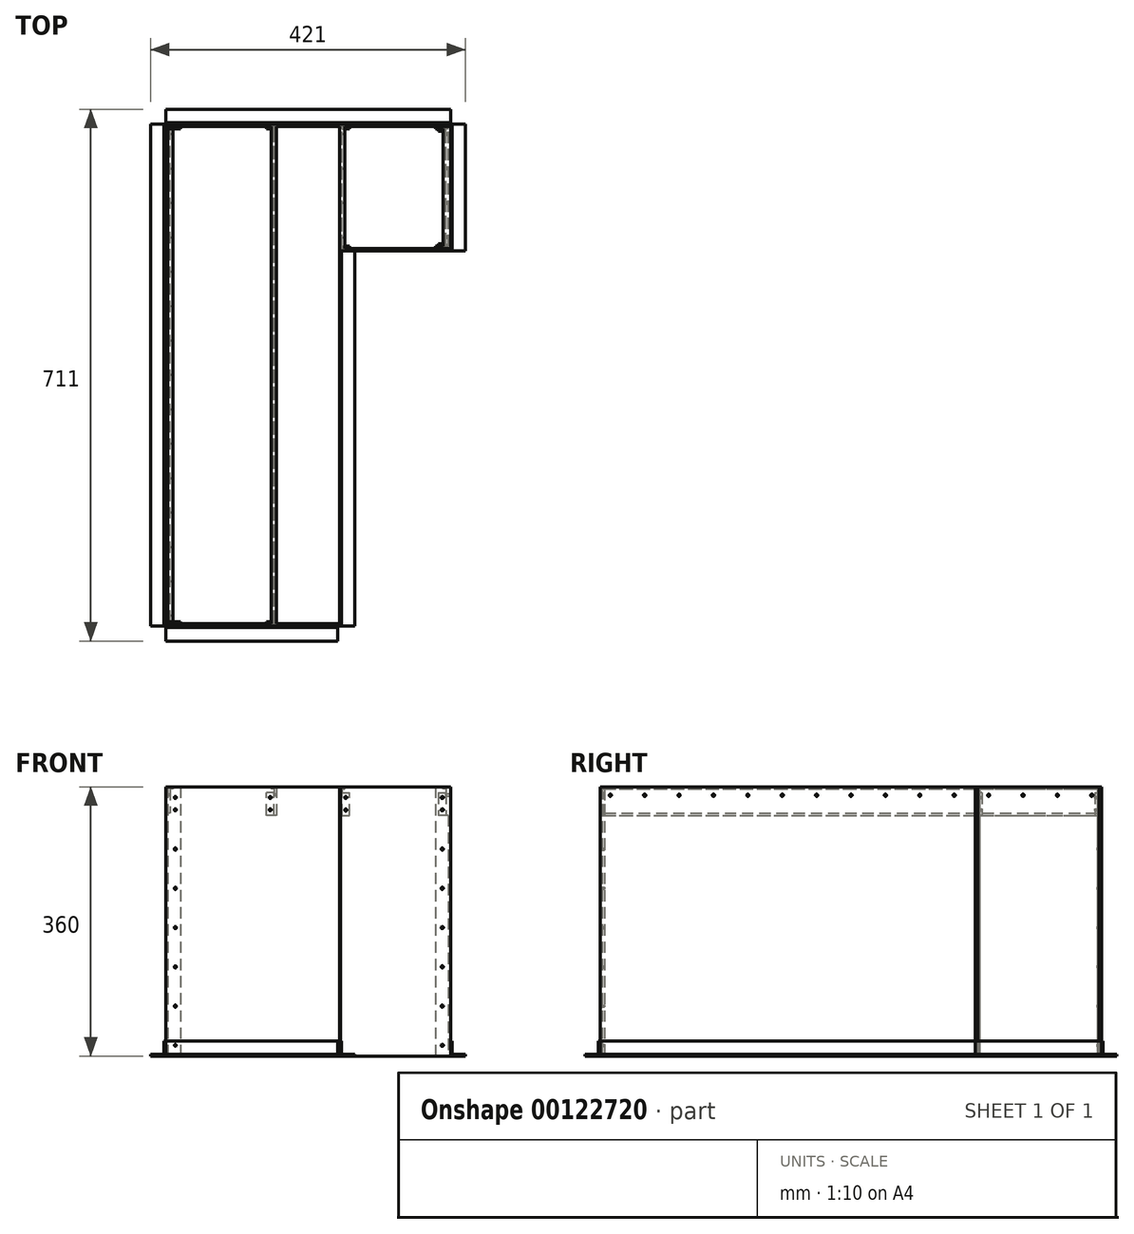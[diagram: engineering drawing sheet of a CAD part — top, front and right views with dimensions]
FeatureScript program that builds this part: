
annotation { "Feature Type Name" : "Feature", "Feature Type Description" : "" }
export const myFeature = defineFeature(function(context is Context, id is Id, definition is map)
    precondition{}
    {
        {
            var Q0;
            Q0=qCreatedBy(makeId("Top.planeOp"),FACE);
            var sketch = newSketch(context, id + "F0", { "sketchPlane" : qUnion([Q0])});
            skLineSegment(sketch, "E0.bottom", {"start": v(0, 0) * mm, "end": v(381, 0) * mm});
            skLineSegment(sketch, "E0.top", {"start": v(0, -3) * mm, "end": v(381, -3) * mm});
            skLineSegment(sketch, "E0.left", {"start": v(0, 0) * mm, "end": v(0, -3) * mm});
            skLineSegment(sketch, "E0.right", {"start": v(381, 0) * mm, "end": v(381, -3) * mm});
            skLineSegment(sketch, "E1.bottom", {"start": v(3, -3) * mm, "end": v(148, -3) * mm, "construction": true});
            skLineSegment(sketch, "E1.top", {"start": v(3, -78) * mm, "end": v(148, -78) * mm, "construction": true});
            skLineSegment(sketch, "E1.left", {"start": v(3, -3) * mm, "end": v(3, -78) * mm, "construction": true});
            skLineSegment(sketch, "E1.right", {"start": v(148, -3) * mm, "end": v(148, -78) * mm, "construction": true});
            skLineSegment(sketch, "E2.bottom", {"start": v(233, -3) * mm, "end": v(378, -3) * mm, "construction": true});
            skLineSegment(sketch, "E2.top", {"start": v(233, -58) * mm, "end": v(378, -58) * mm, "construction": true});
            skLineSegment(sketch, "E2.left", {"start": v(233, -3) * mm, "end": v(233, -58) * mm, "construction": true});
            skLineSegment(sketch, "E2.right", {"start": v(378, -3) * mm, "end": v(378, -58) * mm, "construction": true});
            skSolve(sketch);
        }
        {
            var Q0;
            Q0=qCreatedBy(makeId("Top.planeOp"),FACE);
            var sketch = newSketch(context, id + "F1", { "sketchPlane" : qUnion([Q0])});
            skLineSegment(sketch, "E3.bottom", {"start": v(3, -668) * mm, "end": v(0, -668) * mm});
            skLineSegment(sketch, "E3.top", {"start": v(3, -3) * mm, "end": v(0, -3) * mm});
            skLineSegment(sketch, "E3.left", {"start": v(3, -668) * mm, "end": v(3, -3) * mm});
            skLineSegment(sketch, "E3.right", {"start": v(0, -668) * mm, "end": v(0, -3) * mm});
            skLineSegment(sketch, "E4.bottom", {"start": v(3, -3) * mm, "end": v(20, -3) * mm});
            skLineSegment(sketch, "E4.top", {"start": v(3, -6) * mm, "end": v(20, -6) * mm});
            skLineSegment(sketch, "E4.left", {"start": v(3, -3) * mm, "end": v(3, -6) * mm});
            skLineSegment(sketch, "E4.right", {"start": v(20, -3) * mm, "end": v(20, -6) * mm});
            skLineSegment(sketch, "E5.bottom", {"start": v(3, -668) * mm, "end": v(20, -668) * mm});
            skLineSegment(sketch, "E5.top", {"start": v(3, -665) * mm, "end": v(20, -665) * mm});
            skLineSegment(sketch, "E5.left", {"start": v(3, -668) * mm, "end": v(3, -665) * mm});
            skLineSegment(sketch, "E5.right", {"start": v(20, -668) * mm, "end": v(20, -665) * mm});
            skSolve(sketch);
        }
        {
            var Q0;
            Q0=qCreatedBy(makeId("Top.planeOp"),FACE);
            var sketch = newSketch(context, id + "F2", { "sketchPlane" : qUnion([Q0])});
            skLineSegment(sketch, "E6.bottom", {"start": v(148, -3) * mm, "end": v(233, -3) * mm});
            skLineSegment(sketch, "E6.top", {"start": v(148, -399) * mm, "end": v(233, -399) * mm});
            skLineSegment(sketch, "E6.left", {"start": v(148, -3) * mm, "end": v(148, -399) * mm});
            skLineSegment(sketch, "E6.right", {"start": v(233, -3) * mm, "end": v(233, -399) * mm});
            skLineSegment(sketch, "E7.bottom", {"start": v(161.5, -6) * mm, "end": v(219.5, -6) * mm, "construction": true});
            skLineSegment(sketch, "E7.top", {"start": v(161.5, -67) * mm, "end": v(219.5, -67) * mm, "construction": true});
            skLineSegment(sketch, "E7.left", {"start": v(161.5, -6) * mm, "end": v(161.5, -67) * mm, "construction": true});
            skLineSegment(sketch, "E7.right", {"start": v(219.5, -6) * mm, "end": v(219.5, -67) * mm, "construction": true});
            skLineSegment(sketch, "E8.bottom", {"start": v(148, -400) * mm, "end": v(233, -400) * mm});
            skLineSegment(sketch, "E8.top", {"start": v(148, -668) * mm, "end": v(233, -668) * mm});
            skLineSegment(sketch, "E8.left", {"start": v(148, -400) * mm, "end": v(148, -668) * mm});
            skLineSegment(sketch, "E8.right", {"start": v(233, -400) * mm, "end": v(233, -668) * mm});
            skSolve(sketch);
        }
        {
            var Q0;
            Q0=qCreatedBy(makeId("Top.planeOp"),FACE);
            var sketch = newSketch(context, id + "F3", { "sketchPlane" : qUnion([Q0])});
            skLineSegment(sketch, "E9.bottom", {"start": v(381, -3) * mm, "end": v(378, -3) * mm});
            skLineSegment(sketch, "E9.top", {"start": v(381, -166) * mm, "end": v(378, -166) * mm});
            skLineSegment(sketch, "E9.left", {"start": v(381, -3) * mm, "end": v(381, -166) * mm});
            skLineSegment(sketch, "E9.right", {"start": v(378, -3) * mm, "end": v(378, -166) * mm});
            skLineSegment(sketch, "E10.bottom", {"start": v(378, -3) * mm, "end": v(361, -3) * mm});
            skLineSegment(sketch, "E10.top", {"start": v(378, -6) * mm, "end": v(361, -6) * mm});
            skLineSegment(sketch, "E10.left", {"start": v(378, -3) * mm, "end": v(378, -6) * mm});
            skLineSegment(sketch, "E10.right", {"start": v(361, -3) * mm, "end": v(361, -6) * mm});
            skLineSegment(sketch, "E11.bottom", {"start": v(378, -166) * mm, "end": v(361, -166) * mm});
            skLineSegment(sketch, "E11.top", {"start": v(378, -163) * mm, "end": v(361, -163) * mm});
            skLineSegment(sketch, "E11.left", {"start": v(378, -166) * mm, "end": v(378, -163) * mm});
            skLineSegment(sketch, "E11.right", {"start": v(361, -166) * mm, "end": v(361, -163) * mm});
            skSolve(sketch);
        }
        {
            var Q0;
            Q0=qCreatedBy(makeId("Top.planeOp"),FACE);
            var sketch = newSketch(context, id + "F4", { "sketchPlane" : qUnion([Q0])});
            skLineSegment(sketch, "E12.bottom", {"start": v(0, -668) * mm, "end": v(233, -668) * mm});
            skLineSegment(sketch, "E12.top", {"start": v(0, -671) * mm, "end": v(233, -671) * mm});
            skLineSegment(sketch, "E12.left", {"start": v(0, -668) * mm, "end": v(0, -671) * mm});
            skLineSegment(sketch, "E12.right", {"start": v(233, -668) * mm, "end": v(233, -671) * mm});
            skSolve(sketch);
        }
        {
            var Q0;
            Q0=qCreatedBy(makeId("Top.planeOp"),FACE);
            var sketch = newSketch(context, id + "F5", { "sketchPlane" : qUnion([Q0])});
            skLineSegment(sketch, "E13.bottom", {"start": v(233, -166) * mm, "end": v(381, -166) * mm});
            skLineSegment(sketch, "E13.top", {"start": v(233, -169) * mm, "end": v(381, -169) * mm});
            skLineSegment(sketch, "E13.left", {"start": v(233, -166) * mm, "end": v(233, -169) * mm});
            skLineSegment(sketch, "E13.right", {"start": v(381, -166) * mm, "end": v(381, -169) * mm});
            skSolve(sketch);
        }
        {
            var Q0;
            Q0=qCreatedBy(makeId("Top.planeOp"),FACE);
            var sketch = newSketch(context, id + "F6", { "sketchPlane" : qUnion([Q0])});
            skLineSegment(sketch, "E14.bottom", {"start": v(145, -3) * mm, "end": v(125, -3) * mm});
            skLineSegment(sketch, "E14.top", {"start": v(145, -6) * mm, "end": v(125, -6) * mm});
            skLineSegment(sketch, "E14.left", {"start": v(145, -3) * mm, "end": v(145, -6) * mm});
            skLineSegment(sketch, "E14.right", {"start": v(125, -3) * mm, "end": v(125, -6) * mm});
            skLineSegment(sketch, "E15.bottom", {"start": v(145, -6) * mm, "end": v(142, -6) * mm});
            skLineSegment(sketch, "E15.top", {"start": v(145, -668) * mm, "end": v(142, -668) * mm});
            skLineSegment(sketch, "E15.left", {"start": v(145, -6) * mm, "end": v(145, -668) * mm});
            skLineSegment(sketch, "E15.right", {"start": v(142, -6) * mm, "end": v(142, -668) * mm});
            skLineSegment(sketch, "E16.bottom", {"start": v(142, -668) * mm, "end": v(125, -668) * mm});
            skLineSegment(sketch, "E16.top", {"start": v(142, -665) * mm, "end": v(125, -665) * mm});
            skLineSegment(sketch, "E16.left", {"start": v(142, -668) * mm, "end": v(142, -665) * mm});
            skLineSegment(sketch, "E16.right", {"start": v(125, -668) * mm, "end": v(125, -665) * mm});
            skSolve(sketch);
        }
        {
            var Q0;
            Q0=makeQuery(id+"F0.imprint","IMPRINT",FACE,{"disambiguationData":[TD([[makeQuery(id+"F0.imprint","IMPRINT",EDGE,{"derivedFrom":sQuery(id+"F0.wireOp",EDGE,"E0.bottom")}),-1.0]])]});
            var Q1;
            Q1=makeQuery(id+"F1.imprint","IMPRINT",FACE,{"disambiguationData":[TD([[makeQuery(id+"F1.imprint","IMPRINT",EDGE,{"derivedFrom":sQuery(id+"F1.wireOp",EDGE,"E4.bottom")}),-1.0]])]});
            var Q2;
            Q2=makeQuery(id+"F1.imprint","IMPRINT",FACE,{"disambiguationData":[TD([[makeQuery(id+"F1.imprint","IMPRINT",EDGE,{"derivedFrom":sQuery(id+"F1.wireOp",EDGE,"E5.bottom")}),1.0]])]});
            var Q3;
            Q3=makeQuery(id+"F1.imprint","IMPRINT",FACE,{"disambiguationData":[TD([[makeQuery(id+"F1.imprint","IMPRINT",EDGE,{"derivedFrom":sQuery(id+"F1.wireOp",EDGE,"E3.bottom")}),-1.0]])]});
            var Q4;
            Q4=makeQuery(id+"F3.imprint","IMPRINT",FACE,{"disambiguationData":[TD([[makeQuery(id+"F3.imprint","IMPRINT",EDGE,{"derivedFrom":sQuery(id+"F3.wireOp",EDGE,"E10.bottom")}),1.0]])]});
            var Q5;
            Q5=makeQuery(id+"F3.imprint","IMPRINT",FACE,{"disambiguationData":[TD([[makeQuery(id+"F3.imprint","IMPRINT",EDGE,{"derivedFrom":sQuery(id+"F3.wireOp",EDGE,"E11.bottom")}),-1.0]])]});
            var Q6;
            Q6=makeQuery(id+"F3.imprint","IMPRINT",FACE,{"disambiguationData":[TD([[makeQuery(id+"F3.imprint","IMPRINT",EDGE,{"derivedFrom":sQuery(id+"F3.wireOp",EDGE,"E9.bottom")}),1.0]])]});
            var Q7;
            Q7=makeQuery(id+"F4.imprint","IMPRINT",FACE,{"disambiguationData":[TD([[makeQuery(id+"F4.imprint","IMPRINT",EDGE,{"derivedFrom":sQuery(id+"F4.wireOp",EDGE,"E12.bottom")}),-1.0]])]});
            var Q8;
            Q8=makeQuery(id+"F5.imprint","IMPRINT",FACE,{"disambiguationData":[TD([[makeQuery(id+"F5.imprint","IMPRINT",EDGE,{"derivedFrom":sQuery(id+"F5.wireOp",EDGE,"E13.bottom")}),-1.0]])]});
            extrude(context, id + "F7", {"entities" : qUnion([Q0, Q1, Q2, Q3, Q4, Q5, Q6, Q7, Q8]), "depth" : 360 * mm});
        }
        {
            var Q0;
            Q0=makeQuery(id+"F7.opExtrude","SWEPT_FACE",FACE,{"disambiguationData":[OSD([sQuery(id+"F0.wireOp",EDGE,"E0.bottom")])]});
            var sketch = newSketch(context, id + "F8", { "sketchPlane" : qUnion([Q0])});
            skLineSegment(sketch, "E17.bottom", {"start": v(0, 0) * mm, "end": v(2, 0) * mm});
            skLineSegment(sketch, "E17.top", {"start": v(0, 20) * mm, "end": v(2, 20) * mm});
            skLineSegment(sketch, "E17.left", {"start": v(0, 0) * mm, "end": v(0, 20) * mm});
            skLineSegment(sketch, "E17.right", {"start": v(2, 0) * mm, "end": v(2, 20) * mm});
            skLineSegment(sketch, "E18.bottom", {"start": v(2, 0) * mm, "end": v(20, 0) * mm});
            skLineSegment(sketch, "E18.top", {"start": v(2, 2) * mm, "end": v(20, 2) * mm});
            skLineSegment(sketch, "E18.left", {"start": v(2, 0) * mm, "end": v(2, 2) * mm});
            skLineSegment(sketch, "E18.right", {"start": v(20, 0) * mm, "end": v(20, 2) * mm});
            skSolve(sketch);
        }
        {
            var Q0;
            Q0=qSketchRegion(id+"F8",true);
            extrude(context, id + "F9", {"entities" : qUnion([Q0]), "oppositeDirection" : true, "depth" : 671 * mm});
        }
        {
            var Q0;
            Q0=makeQuery(id+"F7.opExtrude","SWEPT_FACE",FACE,{"disambiguationData":[OSD([sQuery(id+"F1.wireOp",EDGE,"E3.right")])]});
            var sketch = newSketch(context, id + "F10", { "sketchPlane" : qUnion([Q0])});
            skLineSegment(sketch, "E19.bottom", {"start": v(671, 20) * mm, "end": v(673, 20) * mm});
            skLineSegment(sketch, "E19.top", {"start": v(671, 0) * mm, "end": v(673, 0) * mm});
            skLineSegment(sketch, "E19.left", {"start": v(671, 20) * mm, "end": v(671, 0) * mm});
            skLineSegment(sketch, "E19.right", {"start": v(673, 20) * mm, "end": v(673, 0) * mm});
            skLineSegment(sketch, "E20.bottom", {"start": v(673, 0) * mm, "end": v(691, 0) * mm});
            skLineSegment(sketch, "E20.top", {"start": v(673, 2) * mm, "end": v(691, 2) * mm});
            skLineSegment(sketch, "E20.left", {"start": v(673, 0) * mm, "end": v(673, 2) * mm});
            skLineSegment(sketch, "E20.right", {"start": v(691, 0) * mm, "end": v(691, 2) * mm});
            skSolve(sketch);
        }
        {
            var Q0;
            Q0=qSketchRegion(id+"F10",true);
            extrude(context, id + "F11", {"entities" : qUnion([Q0]), "operationType" : NewBodyOperationType.ADD, "oppositeDirection" : true, "depth" : 230 * mm});
        }
        {
            var Q0;
            Q0=makeQuery(id+"F7.opExtrude","SWEPT_FACE",FACE,{"disambiguationData":[OSD([sQuery(id+"F4.wireOp",EDGE,"E12.top")])]});
            var sketch = newSketch(context, id + "F12", { "sketchPlane" : qUnion([Q0])});
            skLineSegment(sketch, "E21.bottom", {"start": v(233, 0) * mm, "end": v(235, 0) * mm});
            skLineSegment(sketch, "E21.top", {"start": v(233, 20) * mm, "end": v(235, 20) * mm});
            skLineSegment(sketch, "E21.left", {"start": v(233, 0) * mm, "end": v(233, 20) * mm});
            skLineSegment(sketch, "E21.right", {"start": v(235, 0) * mm, "end": v(235, 20) * mm});
            skLineSegment(sketch, "E22.bottom", {"start": v(235, 0) * mm, "end": v(253, 0) * mm});
            skLineSegment(sketch, "E22.top", {"start": v(235, 2) * mm, "end": v(253, 2) * mm});
            skLineSegment(sketch, "E22.left", {"start": v(235, 0) * mm, "end": v(235, 2) * mm});
            skLineSegment(sketch, "E22.right", {"start": v(253, 0) * mm, "end": v(253, 2) * mm});
            skSolve(sketch);
        }
        {
            var Q0;
            Q0=qSketchRegion(id+"F12",true);
            extrude(context, id + "F13", {"entities" : qUnion([Q0]), "oppositeDirection" : true, "depth" : 502 * mm});
        }
        {
            var Q0;
            Q0=makeQuery(id+"F7.opExtrude","SWEPT_FACE",FACE,{"disambiguationData":[OSD([sQuery(id+"F5.wireOp",EDGE,"E13.top")])]});
            var sketch = newSketch(context, id + "F14", { "sketchPlane" : qUnion([Q0])});
            skLineSegment(sketch, "E23.bottom", {"start": v(381, 0) * mm, "end": v(383, 0) * mm});
            skLineSegment(sketch, "E23.top", {"start": v(381, 20) * mm, "end": v(383, 20) * mm});
            skLineSegment(sketch, "E23.left", {"start": v(381, 0) * mm, "end": v(381, 20) * mm});
            skLineSegment(sketch, "E23.right", {"start": v(383, 0) * mm, "end": v(383, 20) * mm});
            skLineSegment(sketch, "E24.bottom", {"start": v(383, 0) * mm, "end": v(401, 0) * mm});
            skLineSegment(sketch, "E24.top", {"start": v(383, 2) * mm, "end": v(401, 2) * mm});
            skLineSegment(sketch, "E24.left", {"start": v(383, 0) * mm, "end": v(383, 2) * mm});
            skLineSegment(sketch, "E24.right", {"start": v(401, 0) * mm, "end": v(401, 2) * mm});
            skSolve(sketch);
        }
        {
            var Q0;
            Q0=qSketchRegion(id+"F14",true);
            extrude(context, id + "F15", {"entities" : qUnion([Q0]), "oppositeDirection" : true, "depth" : 169 * mm});
        }
        {
            var Q0;
            Q0=makeQuery(id+"F7.opExtrude","SWEPT_FACE",FACE,{"disambiguationData":[OSD([sQuery(id+"F0.wireOp",EDGE,"E0.right")])]});
            var sketch = newSketch(context, id + "F16", { "sketchPlane" : qUnion([Q0])});
            skLineSegment(sketch, "E25.bottom", {"start": v(0, 0) * mm, "end": v(2, 0) * mm});
            skLineSegment(sketch, "E25.top", {"start": v(0, 20) * mm, "end": v(2, 20) * mm});
            skLineSegment(sketch, "E25.left", {"start": v(0, 0) * mm, "end": v(0, 20) * mm});
            skLineSegment(sketch, "E25.right", {"start": v(2, 0) * mm, "end": v(2, 20) * mm});
            skLineSegment(sketch, "E26.bottom", {"start": v(2, 0) * mm, "end": v(20, 0) * mm});
            skLineSegment(sketch, "E26.top", {"start": v(2, 2) * mm, "end": v(20, 2) * mm});
            skLineSegment(sketch, "E26.left", {"start": v(2, 0) * mm, "end": v(2, 2) * mm});
            skLineSegment(sketch, "E26.right", {"start": v(20, 0) * mm, "end": v(20, 2) * mm});
            skSolve(sketch);
        }
        {
            var Q0;
            Q0=qSketchRegion(id+"F16",true);
            extrude(context, id + "F17", {"entities" : qUnion([Q0]), "oppositeDirection" : true, "depth" : 381 * mm});
        }
        {
            var Q0;
            Q0=makeQuery(id+"F7.opExtrude","CAP_FACE",FACE,{"disambiguationData":[OSD([sQuery(id+"F4.wireOp",EDGE,"E12.bottom"),sQuery(id+"F4.wireOp",EDGE,"E12.top"),sQuery(id+"F4.wireOp",EDGE,"E12.left"),sQuery(id+"F4.wireOp",EDGE,"E12.right")])],"isStart":false});
            var sketch = newSketch(context, id + "F18", { "sketchPlane" : qUnion([Q0])});
            skLineSegment(sketch, "E27.bottom", {"start": v(233, -169) * mm, "end": v(234, -169) * mm});
            skLineSegment(sketch, "E27.top", {"start": v(233, -671) * mm, "end": v(234, -671) * mm});
            skLineSegment(sketch, "E27.left", {"start": v(233, -169) * mm, "end": v(233, -671) * mm});
            skLineSegment(sketch, "E27.right", {"start": v(234, -169) * mm, "end": v(234, -671) * mm});
            skSolve(sketch);
        }
        {
            var Q0;
            Q0=qSketchRegion(id+"F18",true);
            extrude(context, id + "F19", {"entities" : qUnion([Q0]), "oppositeDirection" : true, "depth" : 360 * mm});
        }
        {
            var Q0;
            Q0=makeQuery(id+"F7.opExtrude","SWEPT_FACE",FACE,{"disambiguationData":[OSD([sQuery(id+"F1.wireOp",EDGE,"E4.top")])]});
            var sketch = newSketch(context, id + "F20", { "sketchPlane" : qUnion([Q0])});
            skLineSegment(sketch, "E28.bottom", {"start": v(10, 360) * mm, "end": v(6, 360) * mm});
            skLineSegment(sketch, "E28.top", {"start": v(10, 357) * mm, "end": v(6, 357) * mm});
            skLineSegment(sketch, "E28.left", {"start": v(10, 360) * mm, "end": v(10, 357) * mm});
            skLineSegment(sketch, "E28.right", {"start": v(6, 360) * mm, "end": v(6, 357) * mm});
            skLineSegment(sketch, "E29.bottom", {"start": v(6, 360) * mm, "end": v(3, 360) * mm});
            skLineSegment(sketch, "E29.top", {"start": v(6, 325) * mm, "end": v(3, 325) * mm});
            skLineSegment(sketch, "E29.left", {"start": v(6, 360) * mm, "end": v(6, 325) * mm});
            skLineSegment(sketch, "E29.right", {"start": v(3, 360) * mm, "end": v(3, 325) * mm});
            skSolve(sketch);
        }
        {
            var Q0;
            Q0=qSketchRegion(id+"F20",true);
            extrude(context, id + "F21", {"entities" : qUnion([Q0]), "depth" : 659 * mm});
        }
        {
            var Q0;
            Q0=makeQuery(id+"F7.opExtrude","SWEPT_FACE",FACE,{"disambiguationData":[OSD([sQuery(id+"F0.wireOp",EDGE,"E0.top")])]});
            var sketch = newSketch(context, id + "F22", { "sketchPlane" : qUnion([Q0])});
            skLineSegment(sketch, "E30.bottom", {"start": v(148, 360) * mm, "end": v(141, 360) * mm});
            skLineSegment(sketch, "E30.top", {"start": v(148, 357) * mm, "end": v(141, 357) * mm});
            skLineSegment(sketch, "E30.left", {"start": v(148, 360) * mm, "end": v(148, 357) * mm});
            skLineSegment(sketch, "E30.right", {"start": v(141, 360) * mm, "end": v(141, 357) * mm});
            skLineSegment(sketch, "E31.bottom", {"start": v(148, 357) * mm, "end": v(145, 357) * mm});
            skLineSegment(sketch, "E31.top", {"start": v(148, 322) * mm, "end": v(145, 322) * mm});
            skLineSegment(sketch, "E31.left", {"start": v(148, 357) * mm, "end": v(148, 322) * mm});
            skLineSegment(sketch, "E31.right", {"start": v(145, 357) * mm, "end": v(145, 322) * mm});
            skSolve(sketch);
        }
        {
            var Q0;
            Q0=qSketchRegion(id+"F22",true);
            extrude(context, id + "F23", {"entities" : qUnion([Q0]), "depth" : 665 * mm});
        }
        {
            var Q0;
            Q0=makeQuery(id+"F7.opExtrude","SWEPT_FACE",FACE,{"disambiguationData":[OSD([sQuery(id+"F0.wireOp",EDGE,"E0.top")])]});
            var sketch = newSketch(context, id + "F24", { "sketchPlane" : qUnion([Q0])});
            skLineSegment(sketch, "E32.bottom", {"start": v(145, 322) * mm, "end": v(135, 322) * mm});
            skLineSegment(sketch, "E32.top", {"start": v(145, 352) * mm, "end": v(135, 352) * mm});
            skLineSegment(sketch, "E32.left", {"start": v(145, 322) * mm, "end": v(145, 352) * mm});
            skLineSegment(sketch, "E32.right", {"start": v(135, 322) * mm, "end": v(135, 352) * mm});
            skSolve(sketch);
        }
        {
            var Q0;
            Q0=qSketchRegion(id+"F24",true);
            extrude(context, id + "F25", {"entities" : qUnion([Q0]), "operationType" : NewBodyOperationType.ADD, "depth" : 3 * mm});
        }
        {
            var Q0;
            Q0=makeQuery(id+"F7.opExtrude","SWEPT_FACE",FACE,{"disambiguationData":[OSD([sQuery(id+"F4.wireOp",EDGE,"E12.bottom")])]});
            var sketch = newSketch(context, id + "F26", { "sketchPlane" : qUnion([Q0])});
            skLineSegment(sketch, "E33.bottom", {"start": v(-145, 322) * mm, "end": v(-135, 322) * mm});
            skLineSegment(sketch, "E33.top", {"start": v(-145, 352) * mm, "end": v(-135, 352) * mm});
            skLineSegment(sketch, "E33.left", {"start": v(-145, 322) * mm, "end": v(-145, 352) * mm});
            skLineSegment(sketch, "E33.right", {"start": v(-135, 322) * mm, "end": v(-135, 352) * mm});
            skSolve(sketch);
        }
        {
            var Q0;
            Q0=qSketchRegion(id+"F26",true);
            extrude(context, id + "F27", {"entities" : qUnion([Q0]), "operationType" : NewBodyOperationType.ADD, "depth" : 3 * mm});
        }
        {
            var Q0;
            Q0=makeQuery(id+"F7.opExtrude","SWEPT_FACE",FACE,{"disambiguationData":[OSD([sQuery(id+"F3.wireOp",EDGE,"E10.top")])]});
            var sketch = newSketch(context, id + "F28", { "sketchPlane" : qUnion([Q0])});
            skLineSegment(sketch, "E34.bottom", {"start": v(378, 357) * mm, "end": v(375, 357) * mm});
            skLineSegment(sketch, "E34.top", {"start": v(378, 322) * mm, "end": v(375, 322) * mm});
            skLineSegment(sketch, "E34.left", {"start": v(378, 357) * mm, "end": v(378, 322) * mm});
            skLineSegment(sketch, "E34.right", {"start": v(375, 357) * mm, "end": v(375, 322) * mm});
            skLineSegment(sketch, "E35.bottom", {"start": v(378, 357) * mm, "end": v(371, 357) * mm});
            skLineSegment(sketch, "E35.top", {"start": v(378, 360) * mm, "end": v(371, 360) * mm});
            skLineSegment(sketch, "E35.left", {"start": v(378, 357) * mm, "end": v(378, 360) * mm});
            skLineSegment(sketch, "E35.right", {"start": v(371, 357) * mm, "end": v(371, 360) * mm});
            skSolve(sketch);
        }
        {
            var Q0;
            Q0=qSketchRegion(id+"F28",true);
            extrude(context, id + "F29", {"entities" : qUnion([Q0]), "depth" : 157 * mm});
        }
        {
            var Q0;
            Q0=makeQuery(id+"F7.opExtrude","SWEPT_FACE",FACE,{"disambiguationData":[OSD([sQuery(id+"F3.wireOp",EDGE,"E10.top")])]});
            var sketch = newSketch(context, id + "F30", { "sketchPlane" : qUnion([Q0])});
            skLineSegment(sketch, "E36.bottom", {"start": v(365, 352) * mm, "end": v(375, 352) * mm});
            skLineSegment(sketch, "E36.top", {"start": v(365, 322) * mm, "end": v(375, 322) * mm});
            skLineSegment(sketch, "E36.left", {"start": v(365, 352) * mm, "end": v(365, 322) * mm});
            skLineSegment(sketch, "E36.right", {"start": v(375, 352) * mm, "end": v(375, 322) * mm});
            skSolve(sketch);
        }
        {
            var Q0;
            Q0=qSketchRegion(id+"F30",true);
            extrude(context, id + "F31", {"entities" : qUnion([Q0]), "operationType" : NewBodyOperationType.ADD, "depth" : 3 * mm});
        }
        {
            var Q0;
            Q0=makeQuery(id+"F7.opExtrude","SWEPT_FACE",FACE,{"disambiguationData":[OSD([sQuery(id+"F3.wireOp",EDGE,"E11.top")])]});
            var sketch = newSketch(context, id + "F32", { "sketchPlane" : qUnion([Q0])});
            skLineSegment(sketch, "E37.bottom", {"start": v(-375, 352) * mm, "end": v(-365, 352) * mm});
            skLineSegment(sketch, "E37.top", {"start": v(-375, 322) * mm, "end": v(-365, 322) * mm});
            skLineSegment(sketch, "E37.left", {"start": v(-375, 352) * mm, "end": v(-375, 322) * mm});
            skLineSegment(sketch, "E37.right", {"start": v(-365, 352) * mm, "end": v(-365, 322) * mm});
            skSolve(sketch);
        }
        {
            var Q0;
            Q0=qSketchRegion(id+"F32",true);
            extrude(context, id + "F33", {"entities" : qUnion([Q0]), "operationType" : NewBodyOperationType.ADD, "depth" : 3 * mm});
        }
        {
            var Q0;
            Q0=makeQuery(id+"F7.opExtrude","SWEPT_FACE",FACE,{"disambiguationData":[OSD([sQuery(id+"F0.wireOp",EDGE,"E0.top")])]});
            var sketch = newSketch(context, id + "F34", { "sketchPlane" : qUnion([Q0])});
            skLineSegment(sketch, "E38.bottom", {"start": v(233, 357) * mm, "end": v(236, 357) * mm});
            skLineSegment(sketch, "E38.top", {"start": v(233, 322) * mm, "end": v(236, 322) * mm});
            skLineSegment(sketch, "E38.left", {"start": v(233, 357) * mm, "end": v(233, 322) * mm});
            skLineSegment(sketch, "E38.right", {"start": v(236, 357) * mm, "end": v(236, 322) * mm});
            skLineSegment(sketch, "E39.bottom", {"start": v(233, 357) * mm, "end": v(240, 357) * mm});
            skLineSegment(sketch, "E39.top", {"start": v(233, 360) * mm, "end": v(240, 360) * mm});
            skLineSegment(sketch, "E39.left", {"start": v(233, 357) * mm, "end": v(233, 360) * mm});
            skLineSegment(sketch, "E39.right", {"start": v(240, 357) * mm, "end": v(240, 360) * mm});
            skSolve(sketch);
        }
        {
            var Q0;
            Q0=qSketchRegion(id+"F34",true);
            extrude(context, id + "F35", {"entities" : qUnion([Q0]), "depth" : 163 * mm});
        }
        {
            var Q0;
            Q0=makeQuery(id+"F34.imprint","IMPRINT",FACE,{"disambiguationData":[TD([[makeQuery(id+"F34.imprint","IMPRINT",EDGE,{"derivedFrom":sQuery(id+"F34.wireOp",EDGE,"E38.top")}),-1.0]])]});
            var sketch = newSketch(context, id + "F36", { "sketchPlane" : qUnion([Q0])});
            skLineSegment(sketch, "E40.bottom", {"start": v(236, 322) * mm, "end": v(246, 322) * mm});
            skLineSegment(sketch, "E40.top", {"start": v(236, 352) * mm, "end": v(246, 352) * mm});
            skLineSegment(sketch, "E40.left", {"start": v(236, 322) * mm, "end": v(236, 352) * mm});
            skLineSegment(sketch, "E40.right", {"start": v(246, 322) * mm, "end": v(246, 352) * mm});
            skSolve(sketch);
        }
        {
            var Q0;
            Q0=makeQuery(id+"F36.imprint","IMPRINT",FACE,{"disambiguationData":[TD([[makeQuery(id+"F36.imprint","IMPRINT",EDGE,{"derivedFrom":sQuery(id+"F36.wireOp",EDGE,"E40.bottom")}),1.0]])]});
            extrude(context, id + "F37", {"entities" : qUnion([Q0]), "operationType" : NewBodyOperationType.ADD, "depth" : 3 * mm});
        }
        {
            var Q0;
            Q0=makeQuery(id+"F7.opExtrude","SWEPT_FACE",FACE,{"disambiguationData":[OSD([sQuery(id+"F5.wireOp",EDGE,"E13.bottom")])]});
            var sketch = newSketch(context, id + "F38", { "sketchPlane" : qUnion([Q0])});
            skLineSegment(sketch, "E41.bottom", {"start": v(-236, 322) * mm, "end": v(-246, 322) * mm});
            skLineSegment(sketch, "E41.top", {"start": v(-236, 352) * mm, "end": v(-246, 352) * mm});
            skLineSegment(sketch, "E41.left", {"start": v(-236, 322) * mm, "end": v(-236, 352) * mm});
            skLineSegment(sketch, "E41.right", {"start": v(-246, 322) * mm, "end": v(-246, 352) * mm});
            skSolve(sketch);
        }
        {
            var Q0;
            Q0=qSketchRegion(id+"F38",true);
            extrude(context, id + "F39", {"entities" : qUnion([Q0]), "operationType" : NewBodyOperationType.ADD, "depth" : 3 * mm});
        }
        {
            var Q0;
            {var subQ0=sQuery(id+"F1.wireOp",EDGE,"E3.right");Q0=makeQuery(id+"F10.imprint","IMPRINT",FACE,{"disambiguationData":[TD([[makeQuery(id+"F10.imprint","IMPRINT",EDGE,{"derivedFrom":makeQuery(id+"F7.opExtrude","CAP_EDGE",EDGE,{"disambiguationData":[OSD([subQ0])],"isStart":true})}),-1.0]])]});}
            var sketch = newSketch(context, id + "F40", { "sketchPlane" : qUnion([Q0])});
            skCircle(sketch, "E42", {"center": v(13.25, 348.75) * mm, "radius": 1.25 * mm});
            skCircle(sketch, "E43", {"center": v(59.25, 348.75) * mm, "radius": 1.25 * mm});
            skCircle(sketch, "E44", {"center": v(105.25, 348.75) * mm, "radius": 1.25 * mm});
            skCircle(sketch, "E45", {"center": v(151.25, 348.75) * mm, "radius": 1.25 * mm});
            skCircle(sketch, "E46", {"center": v(197.25, 348.75) * mm, "radius": 1.25 * mm});
            skCircle(sketch, "E47", {"center": v(243.25, 348.75) * mm, "radius": 1.25 * mm});
            skCircle(sketch, "E48", {"center": v(289.25, 348.75) * mm, "radius": 1.25 * mm});
            skCircle(sketch, "E49", {"center": v(335.25, 348.75) * mm, "radius": 1.25 * mm});
            skCircle(sketch, "E50", {"center": v(381.25, 348.75) * mm, "radius": 1.25 * mm});
            skCircle(sketch, "E51", {"center": v(427.25, 348.75) * mm, "radius": 1.25 * mm});
            skCircle(sketch, "E52", {"center": v(473.25, 348.75) * mm, "radius": 1.25 * mm});
            skCircle(sketch, "E53", {"center": v(519.25, 348.75) * mm, "radius": 1.25 * mm});
            skCircle(sketch, "E54", {"center": v(565.25, 348.75) * mm, "radius": 1.25 * mm});
            skCircle(sketch, "E55", {"center": v(611.25, 348.75) * mm, "radius": 1.25 * mm});
            skCircle(sketch, "E56", {"center": v(657.25, 348.75) * mm, "radius": 1.25 * mm});
            skSolve(sketch);
        }
        {
            var Q0;
            {var subQ3=sQuery(id+"F8.wireOp",EDGE,"E17.left");Q0=makeQuery(id+"F8.imprint","IMPRINT",FACE,{"disambiguationData":[TD([[makeQuery(id+"F8.imprint","IMPRINT",EDGE,{"derivedFrom":subQ3}),-1.0]])]});}
            var sketch = newSketch(context, id + "F41", { "sketchPlane" : qUnion([Q0])});
            skCircle(sketch, "E57", {"center": v(-370, 345.75) * mm, "radius": 1.25 * mm});
            skCircle(sketch, "E58", {"center": v(-370, 329.25) * mm, "radius": 1.25 * mm});
            skCircle(sketch, "E59", {"center": v(-370, 276.75) * mm, "radius": 1.25 * mm});
            skCircle(sketch, "E60", {"center": v(-370, 224.25) * mm, "radius": 1.25 * mm});
            skCircle(sketch, "E61", {"center": v(-370, 171.75) * mm, "radius": 1.25 * mm});
            skCircle(sketch, "E62", {"center": v(-370, 119.25) * mm, "radius": 1.25 * mm});
            skCircle(sketch, "E63", {"center": v(-370, 66.75) * mm, "radius": 1.25 * mm});
            skCircle(sketch, "E64", {"center": v(-370, 14.25) * mm, "radius": 1.25 * mm});
            skCircle(sketch, "E65", {"center": v(-13, 345.75) * mm, "radius": 1.25 * mm});
            skCircle(sketch, "E66", {"center": v(-13, 329.25) * mm, "radius": 1.25 * mm});
            skCircle(sketch, "E67", {"center": v(-13, 276.75) * mm, "radius": 1.25 * mm});
            skCircle(sketch, "E68", {"center": v(-13, 224.25) * mm, "radius": 1.25 * mm});
            skCircle(sketch, "E69", {"center": v(-13, 171.75) * mm, "radius": 1.25 * mm});
            skCircle(sketch, "E70", {"center": v(-13, 119.25) * mm, "radius": 1.25 * mm});
            skCircle(sketch, "E71", {"center": v(-13, 66.75) * mm, "radius": 1.25 * mm});
            skCircle(sketch, "E72", {"center": v(-13, 14.25) * mm, "radius": 1.25 * mm});
            skCircle(sketch, "E73", {"center": v(-140, 345.75) * mm, "radius": 1.25 * mm});
            skCircle(sketch, "E74", {"center": v(-140, 329.25) * mm, "radius": 1.25 * mm});
            skCircle(sketch, "E75", {"center": v(-241, 345.75) * mm, "radius": 1.25 * mm});
            skCircle(sketch, "E76", {"center": v(-241, 329) * mm, "radius": 1.25 * mm});
            skSolve(sketch);
        }
        {
            var Q0;
            Q0=qSketchRegion(id+"F41",true);
            extrude(context, id + "F42", {"entities" : qUnion([Q0]), "operationType" : NewBodyOperationType.REMOVE, "endBound" : BoundingType.THROUGH_ALL, "oppositeDirection" : true, "depth" : 25 * mm});
        }
        {
            var Q0;
            Q0=sQuery(id+"F41.wireOp",VERTEX,"E57.center");
            var Q1;
            Q1=sQuery(id+"F41.wireOp",VERTEX,"E58.center");
            var Q2;
            Q2=sQuery(id+"F41.wireOp",VERTEX,"E59.center");
            var Q3;
            Q3=sQuery(id+"F41.wireOp",VERTEX,"E60.center");
            var Q4;
            Q4=sQuery(id+"F41.wireOp",VERTEX,"E61.center");
            var Q5;
            Q5=sQuery(id+"F41.wireOp",VERTEX,"E62.center");
            var Q6;
            Q6=sQuery(id+"F41.wireOp",VERTEX,"E63.center");
            var Q7;
            Q7=sQuery(id+"F41.wireOp",VERTEX,"E64.center");
            var Q8;
            Q8=sQuery(id+"F41.wireOp",VERTEX,"E75.center");
            var Q9;
            Q9=sQuery(id+"F41.wireOp",VERTEX,"E76.center");
            var Q10;
            Q10=sQuery(id+"F41.wireOp",VERTEX,"E73.center");
            var Q11;
            Q11=sQuery(id+"F41.wireOp",VERTEX,"E74.center");
            var Q12;
            Q12=sQuery(id+"F41.wireOp",VERTEX,"E65.center");
            var Q13;
            Q13=sQuery(id+"F41.wireOp",VERTEX,"E66.center");
            var Q14;
            Q14=sQuery(id+"F41.wireOp",VERTEX,"E67.center");
            var Q15;
            Q15=sQuery(id+"F41.wireOp",VERTEX,"E68.center");
            var Q16;
            Q16=sQuery(id+"F41.wireOp",VERTEX,"E69.center");
            var Q17;
            Q17=sQuery(id+"F41.wireOp",VERTEX,"E70.center");
            var Q18;
            Q18=sQuery(id+"F41.wireOp",VERTEX,"E71.center");
            var Q19;
            Q19=sQuery(id+"F44.wireOp",VERTEX,"E84.center");
            var Q20;
            Q20=makeQuery(id+"F7.opExtrude","SWEPT_BODY",BODY,{"disambiguationData":[OSD([sQuery(id+"F0.wireOp",EDGE,"E0.bottom"),sQuery(id+"F0.wireOp",EDGE,"E0.top"),sQuery(id+"F0.wireOp",EDGE,"E0.left"),sQuery(id+"F0.wireOp",EDGE,"E0.right")])]});
            var Q21;
            Q21=makeQuery(id+"F17.opExtrude","SWEPT_BODY",BODY,{"disambiguationData":[OSD([sQuery(id+"F16.wireOp",EDGE,"E25.bottom"),sQuery(id+"F16.wireOp",EDGE,"E25.top"),sQuery(id+"F16.wireOp",EDGE,"E25.left"),sQuery(id+"F16.wireOp",EDGE,"E25.right"),sQuery(id+"F16.wireOp",EDGE,"E26.bottom"),sQuery(id+"F16.wireOp",EDGE,"E26.top"),sQuery(id+"F16.wireOp",EDGE,"E26.right")])]});
            var Q22;
            Q22=makeQuery(id+"F7.opExtrude","SWEPT_BODY",BODY,{"disambiguationData":[OSD([sQuery(id+"F5.wireOp",EDGE,"E13.bottom"),sQuery(id+"F5.wireOp",EDGE,"E13.top"),sQuery(id+"F5.wireOp",EDGE,"E13.left"),sQuery(id+"F5.wireOp",EDGE,"E13.right")])]});
            var Q23;
            Q23=makeQuery(id+"F7.opExtrude","SWEPT_BODY",BODY,{"disambiguationData":[OSD([sQuery(id+"F4.wireOp",EDGE,"E12.bottom"),sQuery(id+"F4.wireOp",EDGE,"E12.top"),sQuery(id+"F4.wireOp",EDGE,"E12.left"),sQuery(id+"F4.wireOp",EDGE,"E12.right")])]});
            var Q24;
            Q24=makeQuery(id+"F7.opExtrude","SWEPT_BODY",BODY,{"disambiguationData":[OSD([sQuery(id+"F2.wireOp",EDGE,"E8.bottom"),sQuery(id+"F2.wireOp",EDGE,"E8.top"),sQuery(id+"F2.wireOp",EDGE,"E8.left"),sQuery(id+"F2.wireOp",EDGE,"E8.right")])]});
            var Q25;
            Q25=makeQuery(id+"F7.opExtrude","SWEPT_BODY",BODY,{"disambiguationData":[OSD([sQuery(id+"F2.wireOp",EDGE,"E6.bottom"),sQuery(id+"F2.wireOp",EDGE,"E6.top"),sQuery(id+"F2.wireOp",EDGE,"E6.left"),sQuery(id+"F2.wireOp",EDGE,"E6.right")])]});
            var Q26;
            Q26=makeQuery(id+"F7.opExtrude","SWEPT_BODY",BODY,{"disambiguationData":[OSD([sQuery(id+"F3.wireOp",EDGE,"E9.bottom"),sQuery(id+"F3.wireOp",EDGE,"E9.top"),sQuery(id+"F3.wireOp",EDGE,"E9.left"),sQuery(id+"F3.wireOp",EDGE,"E9.right"),sQuery(id+"F3.wireOp",EDGE,"E10.bottom"),sQuery(id+"F3.wireOp",EDGE,"E10.top"),sQuery(id+"F3.wireOp",EDGE,"E10.right"),sQuery(id+"F3.wireOp",EDGE,"E11.bottom"),sQuery(id+"F3.wireOp",EDGE,"E11.top"),sQuery(id+"F3.wireOp",EDGE,"E11.right")])]});
            hole(context, id + "F43", {"style" : HoleStyle.SIMPLE, "endStyle" : HoleEndStyle.THROUGH, "holeDiameter" : 3 * mm, "locations" : qUnion([Q0, Q1, Q2, Q3, Q4, Q5, Q6, Q7, Q8, Q9, Q10, Q11, Q12, Q13, Q14, Q15, Q16, Q17, Q18, Q19]), "scope" : qUnion([Q20, Q21, Q22, Q23, Q24, Q25, Q26]), "isTappedThrough" : true});
        }
        {
            var Q0;
            Q0=makeQuery(id+"F17.opExtrude","SWEPT_FACE",FACE,{"disambiguationData":[OSD([sQuery(id+"F16.wireOp",EDGE,"E25.right")])]});
            var sketch = newSketch(context, id + "F44", { "sketchPlane" : qUnion([Q0])});
            skCircle(sketch, "E77", {"center": v(-370, 14.25) * mm, "radius": 1.5 * mm});
            skCircle(sketch, "E78", {"center": v(-319, 14.25) * mm, "radius": 1.5 * mm});
            skCircle(sketch, "E79", {"center": v(-268, 14.25) * mm, "radius": 1.5 * mm});
            skCircle(sketch, "E80", {"center": v(-217, 14.25) * mm, "radius": 1.5 * mm});
            skCircle(sketch, "E81", {"center": v(-166, 14.25) * mm, "radius": 1.5 * mm});
            skCircle(sketch, "E82", {"center": v(-115, 14.25) * mm, "radius": 1.5 * mm});
            skCircle(sketch, "E83", {"center": v(-64, 14.25) * mm, "radius": 1.5 * mm});
            skCircle(sketch, "E84", {"center": v(-13, 14.25) * mm, "radius": 1.5 * mm});
            skSolve(sketch);
        }
        {
            var Q0;
            Q0=sQuery(id+"F40.wireOp",VERTEX,"E42.center");
            var Q1;
            Q1=sQuery(id+"F40.wireOp",VERTEX,"E43.center");
            var Q2;
            Q2=sQuery(id+"F40.wireOp",VERTEX,"E44.center");
            var Q3;
            Q3=sQuery(id+"F40.wireOp",VERTEX,"E45.center");
            var Q4;
            Q4=sQuery(id+"F40.wireOp",VERTEX,"E46.center");
            var Q5;
            Q5=sQuery(id+"F40.wireOp",VERTEX,"E47.center");
            var Q6;
            Q6=sQuery(id+"F40.wireOp",VERTEX,"E48.center");
            var Q7;
            Q7=sQuery(id+"F40.wireOp",VERTEX,"E49.center");
            var Q8;
            Q8=sQuery(id+"F40.wireOp",VERTEX,"E50.center");
            var Q9;
            Q9=sQuery(id+"F40.wireOp",VERTEX,"E51.center");
            var Q10;
            Q10=sQuery(id+"F40.wireOp",VERTEX,"E52.center");
            var Q11;
            Q11=sQuery(id+"F40.wireOp",VERTEX,"E53.center");
            var Q12;
            Q12=sQuery(id+"F40.wireOp",VERTEX,"E54.center");
            var Q13;
            Q13=sQuery(id+"F40.wireOp",VERTEX,"E55.center");
            var Q14;
            Q14=sQuery(id+"F40.wireOp",VERTEX,"E56.center");
            var Q15;
            Q15=makeQuery(id+"F7.opExtrude","SWEPT_BODY",BODY,{"disambiguationData":[OSD([sQuery(id+"F1.wireOp",EDGE,"E3.bottom"),sQuery(id+"F1.wireOp",EDGE,"E3.top"),sQuery(id+"F1.wireOp",EDGE,"E3.left"),sQuery(id+"F1.wireOp",EDGE,"E3.right"),sQuery(id+"F1.wireOp",EDGE,"E4.bottom"),sQuery(id+"F1.wireOp",EDGE,"E4.top"),sQuery(id+"F1.wireOp",EDGE,"E4.right"),sQuery(id+"F1.wireOp",EDGE,"E5.bottom"),sQuery(id+"F1.wireOp",EDGE,"E5.top"),sQuery(id+"F1.wireOp",EDGE,"E5.right")])]});
            var Q16;
            Q16=makeQuery(id+"F7.opExtrude","SWEPT_BODY",BODY,{"disambiguationData":[OSD([sQuery(id+"F3.wireOp",EDGE,"E9.bottom"),sQuery(id+"F3.wireOp",EDGE,"E9.top"),sQuery(id+"F3.wireOp",EDGE,"E9.left"),sQuery(id+"F3.wireOp",EDGE,"E9.right"),sQuery(id+"F3.wireOp",EDGE,"E10.bottom"),sQuery(id+"F3.wireOp",EDGE,"E10.top"),sQuery(id+"F3.wireOp",EDGE,"E10.right"),sQuery(id+"F3.wireOp",EDGE,"E11.bottom"),sQuery(id+"F3.wireOp",EDGE,"E11.top"),sQuery(id+"F3.wireOp",EDGE,"E11.right")])]});
            var Q17;
            Q17=makeQuery(id+"F19.opExtrude","SWEPT_BODY",BODY,{"disambiguationData":[OSD([sQuery(id+"F18.wireOp",EDGE,"E27.bottom"),sQuery(id+"F18.wireOp",EDGE,"E27.top"),sQuery(id+"F18.wireOp",EDGE,"E27.left"),sQuery(id+"F18.wireOp",EDGE,"E27.right")])]});
            var Q18;
            Q18=makeQuery(id+"F7.opExtrude","SWEPT_BODY",BODY,{"disambiguationData":[OSD([sQuery(id+"F2.wireOp",EDGE,"E6.bottom"),sQuery(id+"F2.wireOp",EDGE,"E6.top"),sQuery(id+"F2.wireOp",EDGE,"E6.left"),sQuery(id+"F2.wireOp",EDGE,"E6.right")])]});
            var Q19;
            Q19=makeQuery(id+"F7.opExtrude","SWEPT_BODY",BODY,{"disambiguationData":[OSD([sQuery(id+"F2.wireOp",EDGE,"E8.bottom"),sQuery(id+"F2.wireOp",EDGE,"E8.top"),sQuery(id+"F2.wireOp",EDGE,"E8.left"),sQuery(id+"F2.wireOp",EDGE,"E8.right")])]});
            hole(context, id + "F45", {"style" : HoleStyle.SIMPLE, "endStyle" : HoleEndStyle.THROUGH, "holeDiameter" : 3 * mm, "locations" : qUnion([Q0, Q1, Q2, Q3, Q4, Q5, Q6, Q7, Q8, Q9, Q10, Q11, Q12, Q13, Q14]), "scope" : qUnion([Q15, Q16, Q17, Q18, Q19]), "isTappedThrough" : true});
        }
        {
            var Q0;
            Q0=qSketchRegion(id+"F40",true);
            extrude(context, id + "F46", {"entities" : qUnion([Q0]), "operationType" : NewBodyOperationType.REMOVE, "oppositeDirection" : true, "depth" : 400 * mm});
        }
        {
            var Q0;
            Q0=makeQuery(id+"F7.opExtrude","SWEPT_EDGE",EDGE,{"disambiguationData":[OSD([sQuery(id+"F1.wireOp",EDGE,"E3.top"),sQuery(id+"F1.wireOp",EDGE,"E3.right")])]});
            fillet(context, id + "F47", {"entities" : qUnion([Q0]), "radius" : 4.2 * mm, "tangentPropagation" : true, "allowEdgeOverflow" : false});
        }
    });
